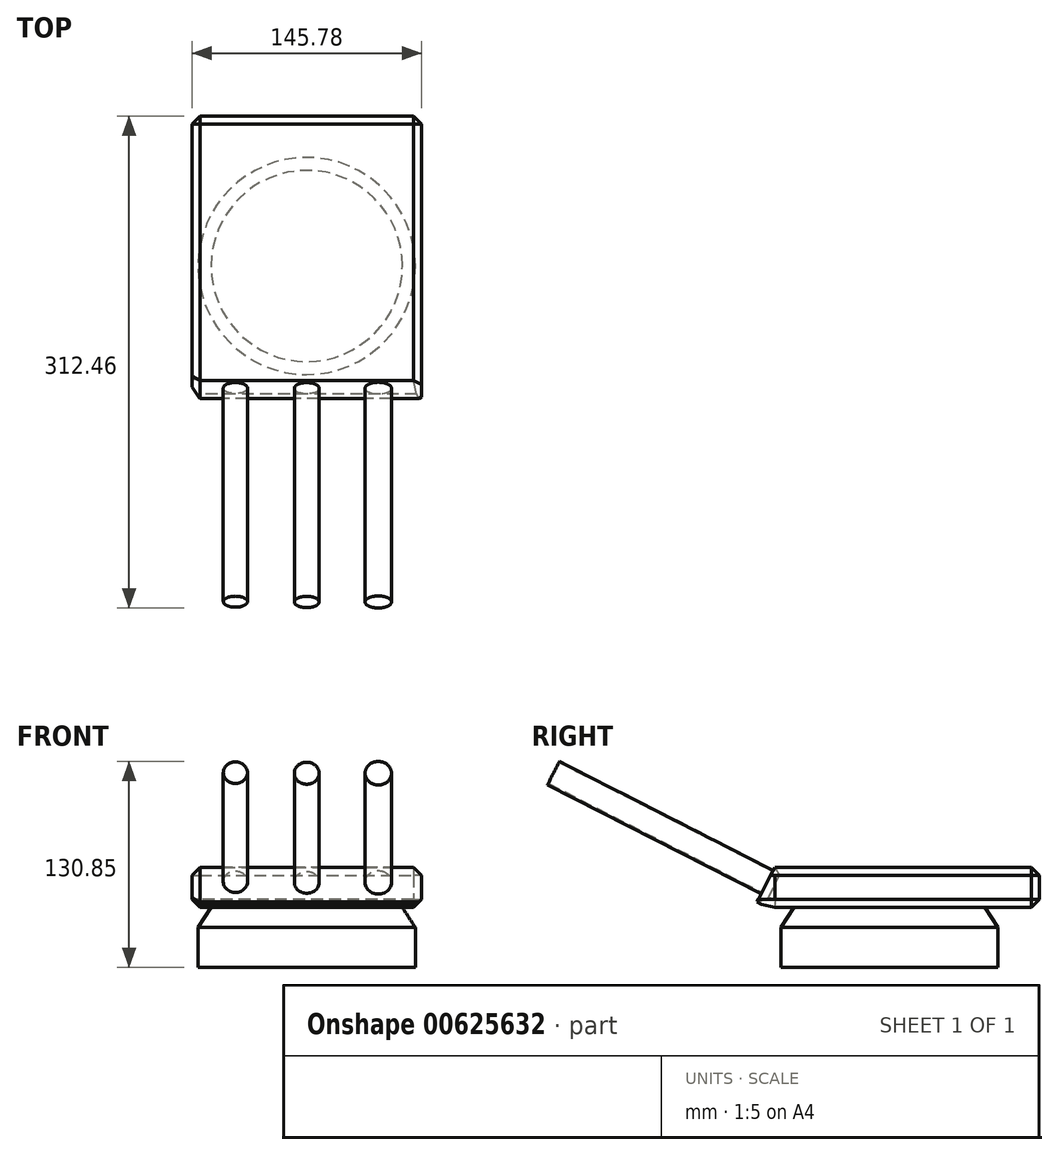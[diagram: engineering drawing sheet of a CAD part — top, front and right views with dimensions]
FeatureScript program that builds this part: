
annotation { "Feature Type Name" : "Feature", "Feature Type Description" : "" }
export const myFeature = defineFeature(function(context is Context, id is Id, definition is map)
    precondition{}
    {
        {
            var Q0;
            Q0=qCreatedBy(makeId("Top.planeOp"),FACE);
            var sketch = newSketch(context, id + "F0", { "sketchPlane" : qUnion([Q0])});
            skCircle(sketch, "E0", {"center": v(0, 0) * mm, "radius": 68.96 * mm});
            skSolve(sketch);
        }
        {
            var Q0;
            Q0 = qSketchRegion(id + "F0", true);
            extrude(context, id + "F1", {"entities" : qUnion([Q0]), "depth" : 25.4 * mm, "offsetDistance" : 25.4 * mm});
        }
        {
            var Q0;
            Q0=qCreatedBy(makeId("Top.planeOp"),FACE);
            cPlane(context, id + "F2", {"entities" : qUnion([Q0]), "cplaneType" : CPlaneType.OFFSET, "offset" : 38.1 * mm, "width" : 152.4 * mm, "height" : 152.4 * mm});
        }
        {
            var Q0;
            Q0=qCreatedBy(id+"F2.planeOp",FACE);
            var sketch = newSketch(context, id + "F3", { "sketchPlane" : qUnion([Q0])});
            skCircle(sketch, "E1", {"center": v(0, 0) * mm, "radius": 60.72 * mm});
            skSolve(sketch);
        }
        {
            var Q1;
            Q1=makeQuery(id+"F1.opExtrude","CAP_FACE",FACE,{"disambiguationData":[OSD([sQuery(id+"F0.wireOp",EDGE,"E0")])],"isStart":false});
            var Q2;
            Q2=makeQuery(id+"F3.imprint","IMPRINT",FACE,{"disambiguationData":[TD([[makeQuery(id+"F3.imprint","IMPRINT",EDGE,{"derivedFrom":sQuery(id+"F3.wireOp",EDGE,"E1")}),1.0]])]});
            loft(context, id + "F4", {"operationType" : NewBodyOperationType.ADD, "sheetProfilesArray" : [{ "sheetProfileEntities" : qUnion([Q1]) }, { "sheetProfileEntities" : qUnion([Q2]) }]});
        }
        {
            var Q0;
            Q0=makeQuery(id+"F4.opLoft","CAP_FACE",FACE,{"disambiguationData":[OSD([makeQuery(id+"F3.imprint","IMPRINT",FACE,{"disambiguationData":[TD([[makeQuery(id+"F3.imprint","IMPRINT",EDGE,{"derivedFrom":sQuery(id+"F3.wireOp",EDGE,"E1")}),1.0]])]})])],"isStart":true});
            cPlane(context, id + "F5", {"entities" : qUnion([Q0]), "cplaneType" : CPlaneType.OFFSET, "offset" : 0 * mm, "width" : 152.4 * mm, "height" : 152.4 * mm});
        }
        {
            var Q0;
            Q0=qCreatedBy(id+"F5.planeOp",FACE);
            var sketch = newSketch(context, id + "F6", { "sketchPlane" : qUnion([Q0])});
            skLineSegment(sketch, "E2.bottom", {"start": v(-72.87, -72.87) * mm, "end": v(72.9, -72.87) * mm});
            skLineSegment(sketch, "E2.top", {"start": v(-72.87, 95.25) * mm, "end": v(72.9, 95.25) * mm});
            skLineSegment(sketch, "E2.left", {"start": v(-72.87, -72.87) * mm, "end": v(-72.87, 95.25) * mm});
            skLineSegment(sketch, "E2.right", {"start": v(72.9, -72.87) * mm, "end": v(72.9, 95.25) * mm});
            skSolve(sketch);
        }
        {
            var Q0;
            Q0 = qSketchRegion(id + "F6", true);
            extrude(context, id + "F7", {"entities" : qUnion([Q0]), "operationType" : NewBodyOperationType.ADD, "depth" : 25.4 * mm, "offsetDistance" : 25.4 * mm});
        }
        {
            var Q0;
            Q0=makeQuery(id+"F7.opExtrude","SWEPT_FACE",FACE,{"disambiguationData":[OSD([sQuery(id+"F6.wireOp",EDGE,"E2.left")])]});
            var sketch = newSketch(context, id + "F8", { "sketchPlane" : qUnion([Q0])});
            skLineSegment(sketch, "E3", {"start": v(72.87, 63.5) * mm, "end": v(84.05, 41.6) * mm});
            skLineSegment(sketch, "E4", {"start": v(84.05, 41.6) * mm, "end": v(81.17, 40.13) * mm});
            skLineSegment(sketch, "E5", {"start": v(81.17, 40.13) * mm, "end": v(72.87, 38.1) * mm});
            skSolve(sketch);
        }
        {
            var Q0;
            Q0=makeQuery(id+"F8.imprint","IMPRINT",FACE,{"disambiguationData":[TD([[makeQuery(id+"F8.imprint","IMPRINT",EDGE,{"derivedFrom":sQuery(id+"F8.wireOp",EDGE,"E3")}),-1.0]])]});
            extrude(context, id + "F9", {"entities" : qUnion([Q0]), "operationType" : NewBodyOperationType.ADD, "oppositeDirection" : true, "depth" : 145.75 * mm, "offsetDistance" : 25.4 * mm});
        }
        {
            var Q0;
            Q0=makeQuery(id+"F9.opExtrude","SWEPT_FACE",FACE,{"disambiguationData":[OSD([sQuery(id+"F8.wireOp",EDGE,"E3")])]});
            var sketch = newSketch(context, id + "F10", { "sketchPlane" : qUnion([Q0])});
            skCircle(sketch, "E6", {"center": v(0, 12.89) * mm, "radius": 7.85 * mm});
            skCircle(sketch, "E7", {"center": v(-45.32, 13.27) * mm, "radius": 7.66 * mm});
            skCircle(sketch, "E8", {"center": v(45.49, 12.89) * mm, "radius": 8.38 * mm});
            skSolve(sketch);
        }
        {
            var Q0;
            Q0=makeQuery(id+"F10.imprint","IMPRINT",FACE,{"disambiguationData":[TD([[makeQuery(id+"F10.imprint","IMPRINT",EDGE,{"derivedFrom":sQuery(id+"F10.wireOp",EDGE,"E7")}),1.0]])]});
            extrude(context, id + "F11", {"entities" : qUnion([Q0]), "operationType" : NewBodyOperationType.ADD, "depth" : 152.4 * mm, "offsetDistance" : 25.4 * mm});
        }
        {
            var Q0;
            Q0=makeQuery(id+"F10.imprint","IMPRINT",FACE,{"disambiguationData":[TD([[makeQuery(id+"F10.imprint","IMPRINT",EDGE,{"derivedFrom":sQuery(id+"F10.wireOp",EDGE,"E6")}),1.0]])]});
            extrude(context, id + "F12", {"entities" : qUnion([Q0]), "operationType" : NewBodyOperationType.ADD, "depth" : 152.4 * mm, "offsetDistance" : 25.4 * mm});
        }
        {
            var Q0;
            Q0=makeQuery(id+"F10.imprint","IMPRINT",FACE,{"disambiguationData":[TD([[makeQuery(id+"F10.imprint","IMPRINT",EDGE,{"derivedFrom":sQuery(id+"F10.wireOp",EDGE,"E8")}),1.0]])]});
            extrude(context, id + "F13", {"entities" : qUnion([Q0]), "operationType" : NewBodyOperationType.ADD, "depth" : 152.4 * mm, "offsetDistance" : 25.4 * mm});
        }
        {
            var Q0;
            Q0=makeQuery(id+"F7.opExtrude","CAP_EDGE",EDGE,{"disambiguationData":[OSD([sQuery(id+"F6.wireOp",EDGE,"E2.right")])],"isStart":true});
            var Q1;
            Q1=makeQuery(id+"F7.opExtrude","CAP_EDGE",EDGE,{"disambiguationData":[OSD([sQuery(id+"F6.wireOp",EDGE,"E2.top")])],"isStart":true});
            var Q2;
            {var subQ0=sQuery(id+"F6.wireOp",EDGE,"E2.left");Q2=makeQuery(id+"F9.boolean.opBoolean","MERGE",FACE,{"derivedFrom":[makeQuery(id+"F7.opExtrude","SWEPT_FACE",FACE,{"disambiguationData":[OSD([subQ0])]}),makeQuery(id+"F9.opExtrude","CAP_FACE",FACE,{"disambiguationData":[OSD([sQuery(id+"F6.wireOp",EDGE,"E2.bottom"),subQ0,sQuery(id+"F8.wireOp",EDGE,"E3"),sQuery(id+"F8.wireOp",EDGE,"E4"),sQuery(id+"F8.wireOp",EDGE,"E5")])],"isStart":true})]});}
            var Q3;
            Q3=makeQuery(id+"F7.opExtrude","CAP_EDGE",EDGE,{"disambiguationData":[OSD([sQuery(id+"F6.wireOp",EDGE,"E2.top")])],"isStart":false});
            var Q4;
            Q4=makeQuery(id+"F7.opExtrude","CAP_EDGE",EDGE,{"disambiguationData":[OSD([sQuery(id+"F6.wireOp",EDGE,"E2.right")])],"isStart":false});
            var Q5;
            Q5=makeQuery(id+"F7.opExtrude","SWEPT_EDGE",EDGE,{"disambiguationData":[OSD([sQuery(id+"F6.wireOp",EDGE,"E2.top"),sQuery(id+"F6.wireOp",EDGE,"E2.right")])]});
            chamfer(context, id + "F14", {"entities" : qUnion([Q0, Q1, Q2, Q3, Q4, Q5]), "width" : 5.08 * mm, "tangentPropagation" : true});
        }
    });
